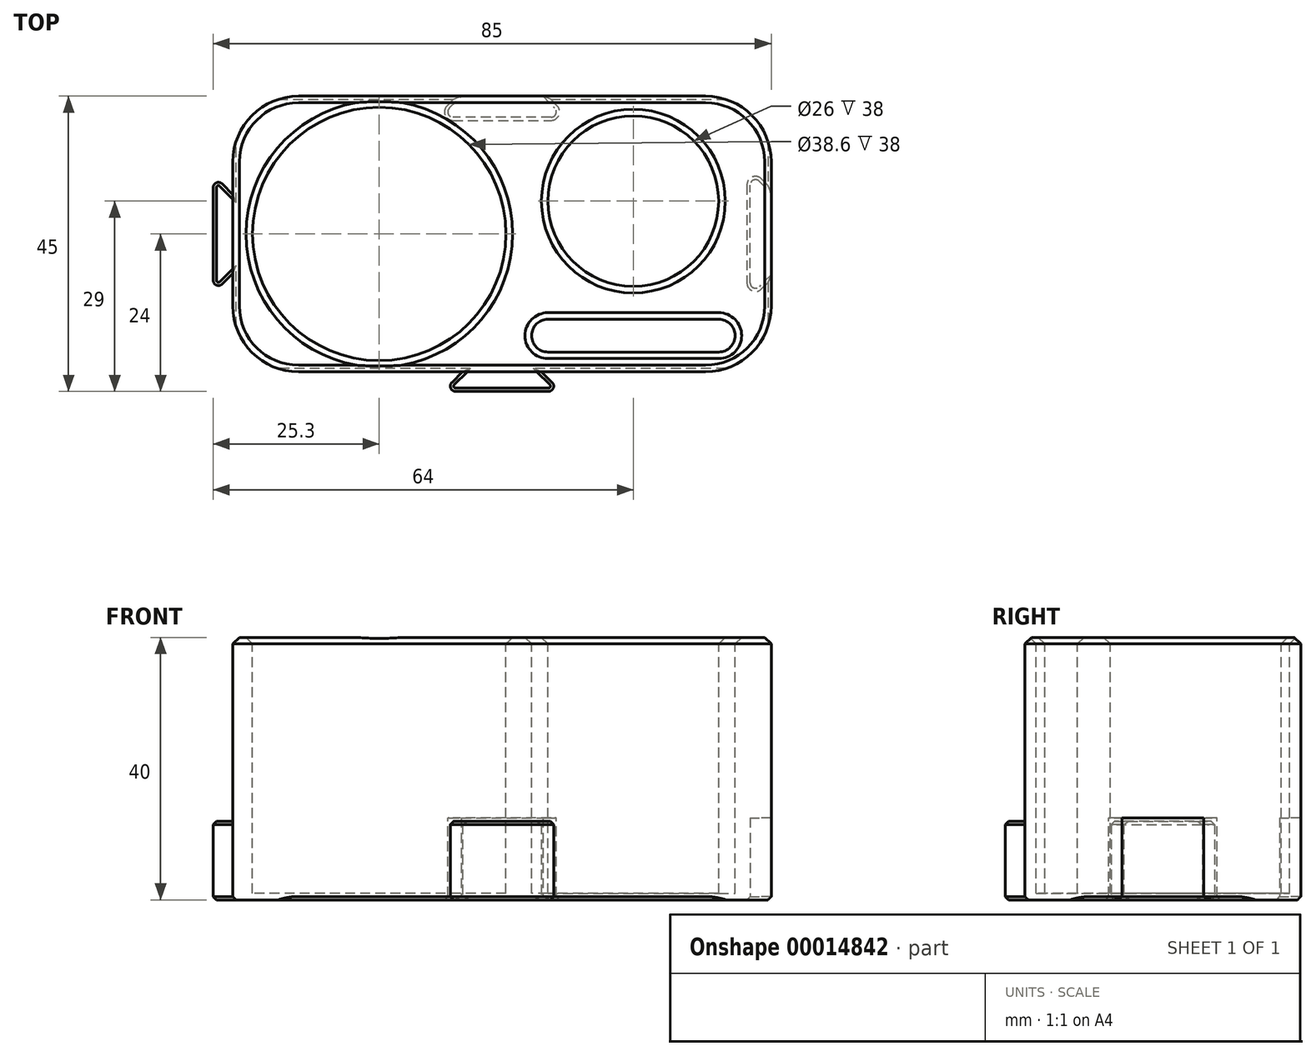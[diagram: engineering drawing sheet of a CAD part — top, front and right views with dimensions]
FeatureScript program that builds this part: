
annotation { "Feature Type Name" : "Feature", "Feature Type Description" : "" }
export const myFeature = defineFeature(function(context is Context, id is Id, definition is map)
    precondition{}
    {
        {
            var Q0;
            Q0=qCreatedBy(makeId("Top.planeOp"),FACE);
            var sketch = newSketch(context, id + "F0", { "sketchPlane" : qUnion([Q0])});
            skLineSegment(sketch, "E0.bottom", {"start": v(0, 0) * mm, "end": v(82, 0) * mm});
            skLineSegment(sketch, "E0.top", {"start": v(0, 42) * mm, "end": v(82, 42) * mm});
            skLineSegment(sketch, "E0.left", {"start": v(0, 0) * mm, "end": v(0, 42) * mm});
            skLineSegment(sketch, "E0.right", {"start": v(82, 0) * mm, "end": v(82, 42) * mm});
            skLineSegment(sketch, "E1", {"start": v(0, 21) * mm, "end": v(82, 21) * mm, "construction": true});
            skLineSegment(sketch, "E2", {"start": v(41, 42) * mm, "end": v(41, 0) * mm, "construction": true});
            skLineSegment(sketch, "E3", {"start": v(35, 0) * mm, "end": v(32, -3) * mm});
            skLineSegment(sketch, "E4", {"start": v(32, -3) * mm, "end": v(50, -3) * mm});
            skLineSegment(sketch, "E5", {"start": v(50, -3) * mm, "end": v(47, 0) * mm});
            skLineSegment(sketch, "E6", {"start": v(47.2, 42) * mm, "end": v(50.4, 38.8) * mm});
            skLineSegment(sketch, "E7", {"start": v(50.4, 38.8) * mm, "end": v(31.6, 38.8) * mm});
            skLineSegment(sketch, "E8", {"start": v(31.6, 38.8) * mm, "end": v(34.8, 42) * mm});
            skLineSegment(sketch, "E9", {"start": v(0, 15) * mm, "end": v(-3, 12) * mm});
            skLineSegment(sketch, "E10", {"start": v(-3, 12) * mm, "end": v(-3, 30) * mm});
            skLineSegment(sketch, "E11", {"start": v(-3, 30) * mm, "end": v(0, 27) * mm});
            skLineSegment(sketch, "E12", {"start": v(82, 14.8) * mm, "end": v(78.8, 11.6) * mm});
            skLineSegment(sketch, "E13", {"start": v(78.8, 11.6) * mm, "end": v(78.8, 30.4) * mm});
            skLineSegment(sketch, "E14", {"start": v(78.8, 30.4) * mm, "end": v(82, 27.2) * mm});
            skSolve(sketch);
        }
        {
            var Q0;
            {var subQ1=sQuery(id+"F0.wireOp",EDGE,"E6");Q0=makeQuery(id+"F0.imprint","IMPRINT",FACE,{"disambiguationData":[TD([[makeQuery(id+"F0.imprint","IMPRINT",EDGE,{"derivedFrom":subQ1}),-1.0]])]});}
            var Q1;
            {var subQ1=sQuery(id+"F0.wireOp",EDGE,"E12");Q1=makeQuery(id+"F0.imprint","IMPRINT",FACE,{"disambiguationData":[TD([[makeQuery(id+"F0.imprint","IMPRINT",EDGE,{"derivedFrom":subQ1}),-1.0]])]});}
            var Q2;
            {var subQ8=sQuery(id+"F0.wireOp",EDGE,"E6");Q2=makeQuery(id+"F0.imprint","IMPRINT",FACE,{"disambiguationData":[TD([[makeQuery(id+"F0.imprint","IMPRINT",EDGE,{"derivedFrom":subQ8}),1.0]])]});}
            extrude(context, id + "F1", {"entities" : qUnion([Q0, Q1, Q2]), "depth" : 40 * mm});
        }
        {
            var Q0;
            {var subQ1=sQuery(id+"F0.wireOp",EDGE,"E3");Q0=makeQuery(id+"F0.imprint","IMPRINT",FACE,{"disambiguationData":[TD([[makeQuery(id+"F0.imprint","IMPRINT",EDGE,{"derivedFrom":subQ1}),1.0]])]});}
            var Q1;
            {var subQ1=sQuery(id+"F0.wireOp",EDGE,"E9");Q1=makeQuery(id+"F0.imprint","IMPRINT",FACE,{"disambiguationData":[TD([[makeQuery(id+"F0.imprint","IMPRINT",EDGE,{"derivedFrom":subQ1}),-1.0]])]});}
            extrude(context, id + "F2", {"entities" : qUnion([Q0, Q1]), "operationType" : NewBodyOperationType.ADD, "depth" : 12 * mm});
        }
        {
            var Q0;
            {var subQ1=sQuery(id+"F0.wireOp",EDGE,"E6");Q0=makeQuery(id+"F0.imprint","IMPRINT",FACE,{"disambiguationData":[TD([[makeQuery(id+"F0.imprint","IMPRINT",EDGE,{"derivedFrom":subQ1}),-1.0]])]});}
            var Q1;
            {var subQ1=sQuery(id+"F0.wireOp",EDGE,"E12");Q1=makeQuery(id+"F0.imprint","IMPRINT",FACE,{"disambiguationData":[TD([[makeQuery(id+"F0.imprint","IMPRINT",EDGE,{"derivedFrom":subQ1}),-1.0]])]});}
            extrude(context, id + "F3", {"entities" : qUnion([Q0, Q1]), "operationType" : NewBodyOperationType.REMOVE, "depth" : 12.5 * mm});
        }
        {
            var Q0;
            Q0=makeQuery(id+"F3.boolean.opBoolean","COPY",EDGE,{"derivedFrom":makeQuery(id+"F3.opExtrude","SWEPT_EDGE",EDGE,{"disambiguationData":[OSD([sQuery(id+"F0.wireOp",EDGE,"E0.right"),sQuery(id+"F0.wireOp",EDGE,"E14")])]})});
            var Q1;
            Q1=makeQuery(id+"F3.boolean.opBoolean","COPY",EDGE,{"derivedFrom":makeQuery(id+"F3.opExtrude","SWEPT_EDGE",EDGE,{"disambiguationData":[OSD([sQuery(id+"F0.wireOp",EDGE,"E13"),sQuery(id+"F0.wireOp",EDGE,"E14")])]})});
            var Q2;
            Q2=makeQuery(id+"F3.boolean.opBoolean","COPY",EDGE,{"derivedFrom":makeQuery(id+"F3.opExtrude","SWEPT_EDGE",EDGE,{"disambiguationData":[OSD([sQuery(id+"F0.wireOp",EDGE,"E0.right"),sQuery(id+"F0.wireOp",EDGE,"E12")])]})});
            var Q3;
            Q3=makeQuery(id+"F2.opExtrude","SWEPT_EDGE",EDGE,{"disambiguationData":[OSD([sQuery(id+"F0.wireOp",EDGE,"E4"),sQuery(id+"F0.wireOp",EDGE,"E5")])]});
            var Q4;
            Q4=makeQuery(id+"F3.boolean.opBoolean","COPY",EDGE,{"derivedFrom":makeQuery(id+"F3.opExtrude","SWEPT_EDGE",EDGE,{"disambiguationData":[OSD([sQuery(id+"F0.wireOp",EDGE,"E12"),sQuery(id+"F0.wireOp",EDGE,"E13")])]})});
            var Q5;
            Q5=makeQuery(id+"F3.boolean.opBoolean","COPY",EDGE,{"derivedFrom":makeQuery(id+"F3.opExtrude","SWEPT_EDGE",EDGE,{"disambiguationData":[OSD([sQuery(id+"F0.wireOp",EDGE,"E0.top"),sQuery(id+"F0.wireOp",EDGE,"E8")])]})});
            var Q6;
            Q6=makeQuery(id+"F3.boolean.opBoolean","COPY",EDGE,{"derivedFrom":makeQuery(id+"F3.opExtrude","SWEPT_EDGE",EDGE,{"disambiguationData":[OSD([sQuery(id+"F0.wireOp",EDGE,"E0.top"),sQuery(id+"F0.wireOp",EDGE,"E6")])]})});
            var Q7;
            Q7=makeQuery(id+"F3.boolean.opBoolean","COPY",EDGE,{"derivedFrom":makeQuery(id+"F3.opExtrude","SWEPT_EDGE",EDGE,{"disambiguationData":[OSD([sQuery(id+"F0.wireOp",EDGE,"E7"),sQuery(id+"F0.wireOp",EDGE,"E8")])]})});
            var Q8;
            Q8=makeQuery(id+"F3.boolean.opBoolean","COPY",EDGE,{"derivedFrom":makeQuery(id+"F3.opExtrude","SWEPT_EDGE",EDGE,{"disambiguationData":[OSD([sQuery(id+"F0.wireOp",EDGE,"E6"),sQuery(id+"F0.wireOp",EDGE,"E7")])]})});
            var Q9;
            Q9=makeQuery(id+"F2.opExtrude","SWEPT_EDGE",EDGE,{"disambiguationData":[OSD([sQuery(id+"F0.wireOp",EDGE,"E10"),sQuery(id+"F0.wireOp",EDGE,"E11")])]});
            var Q10;
            Q10=makeQuery(id+"F2.opExtrude","SWEPT_EDGE",EDGE,{"disambiguationData":[OSD([sQuery(id+"F0.wireOp",EDGE,"E0.left"),sQuery(id+"F0.wireOp",EDGE,"E11")])]});
            var Q11;
            Q11=makeQuery(id+"F2.opExtrude","SWEPT_EDGE",EDGE,{"disambiguationData":[OSD([sQuery(id+"F0.wireOp",EDGE,"E0.left"),sQuery(id+"F0.wireOp",EDGE,"E9")])]});
            var Q12;
            Q12=makeQuery(id+"F2.opExtrude","SWEPT_EDGE",EDGE,{"disambiguationData":[OSD([sQuery(id+"F0.wireOp",EDGE,"E9"),sQuery(id+"F0.wireOp",EDGE,"E10")])]});
            var Q13;
            Q13=makeQuery(id+"F2.opExtrude","SWEPT_EDGE",EDGE,{"disambiguationData":[OSD([sQuery(id+"F0.wireOp",EDGE,"E3"),sQuery(id+"F0.wireOp",EDGE,"E4")])]});
            var Q14;
            Q14=makeQuery(id+"F2.opExtrude","SWEPT_EDGE",EDGE,{"disambiguationData":[OSD([sQuery(id+"F0.wireOp",EDGE,"E0.bottom"),sQuery(id+"F0.wireOp",EDGE,"E3")])]});
            var Q15;
            Q15=makeQuery(id+"F2.opExtrude","SWEPT_EDGE",EDGE,{"disambiguationData":[OSD([sQuery(id+"F0.wireOp",EDGE,"E0.bottom"),sQuery(id+"F0.wireOp",EDGE,"E5")])]});
            fillet(context, id + "F4", {"entities" : qUnion([Q0, Q1, Q2, Q3, Q4, Q5, Q6, Q7, Q8, Q9, Q10, Q11, Q12, Q13, Q14, Q15]), "radius" : .8 * mm, "tangentPropagation" : true, "allowEdgeOverflow" : false});
        }
        {
            var Q0;
            Q0=makeQuery(id+"F2.opExtrude","CAP_EDGE",EDGE,{"disambiguationData":[OSD([sQuery(id+"F0.wireOp",EDGE,"E4")])],"isStart":false});
            var Q1;
            Q1=makeQuery(id+"F2.opExtrude","CAP_EDGE",EDGE,{"disambiguationData":[OSD([sQuery(id+"F0.wireOp",EDGE,"E10")])],"isStart":false});
            chamfer(context, id + "F5", {"entities" : qUnion([Q0, Q1]), "width" : .5 * mm, "tangentPropagation" : true});
        }
        {
            var Q0;
            {var subQ0=sQuery(id+"F0.wireOp",EDGE,"E0.bottom");var subQ1=sQuery(id+"F0.wireOp",EDGE,"E0.left");Q0=makeQuery(id+"F2.boolean.opBoolean","MERGE",FACE,{"derivedFrom":[makeQuery(id+"F1.opExtrude","CAP_FACE",FACE,{"disambiguationData":[OSD([subQ0,sQuery(id+"F0.wireOp",EDGE,"E0.top"),subQ1,sQuery(id+"F0.wireOp",EDGE,"E0.right")])],"isStart":true}),makeQuery(id+"F2.opExtrude","CAP_FACE",FACE,{"disambiguationData":[OSD([subQ0,sQuery(id+"F0.wireOp",EDGE,"E3"),sQuery(id+"F0.wireOp",EDGE,"E4"),sQuery(id+"F0.wireOp",EDGE,"E5")])],"isStart":true}),makeQuery(id+"F2.opExtrude","CAP_FACE",FACE,{"disambiguationData":[OSD([subQ1,sQuery(id+"F0.wireOp",EDGE,"E9"),sQuery(id+"F0.wireOp",EDGE,"E10"),sQuery(id+"F0.wireOp",EDGE,"E11")])],"isStart":true})]});}
            chamfer(context, id + "F6", {"entities" : qUnion([Q0]), "width" : .5 * mm, "tangentPropagation" : true});
        }
        {
            var Q0;
            Q0=makeQuery(id+"F1.opExtrude","CAP_FACE",FACE,{"disambiguationData":[OSD([sQuery(id+"F0.wireOp",EDGE,"E0.bottom"),sQuery(id+"F0.wireOp",EDGE,"E0.top"),sQuery(id+"F0.wireOp",EDGE,"E0.left"),sQuery(id+"F0.wireOp",EDGE,"E0.right")])],"isStart":false});
            var sketch = newSketch(context, id + "F7", { "sketchPlane" : qUnion([Q0])});
            skLineSegment(sketch, "E15", {"start": v(0, 21) * mm, "end": v(82, 21) * mm, "construction": true});
            skCircle(sketch, "E16", {"center": v(22.3, 21) * mm, "radius": 19.3 * mm});
            skLineSegment(sketch, "E17", {"start": v(48, 8) * mm, "end": v(74, 8) * mm});
            skLineSegment(sketch, "E18", {"start": v(74, 3) * mm, "end": v(48, 3) * mm});
            skArc(sketch, "E19", {"start": v(48, 8) * mm, "mid": v(45.5, 5.5) * mm, "end": v(48, 3) * mm});
            skArc(sketch, "E20", {"start": v(74, 3) * mm, "mid": v(76.5, 5.5) * mm, "end": v(74, 8) * mm});
            skCircle(sketch, "E21", {"center": v(61, 26) * mm, "radius": 13 * mm});
            skSolve(sketch);
        }
        {
            var Q0;
            Q0=makeQuery(id+"F7.imprint","IMPRINT",FACE,{"disambiguationData":[TD([[makeQuery(id+"F7.imprint","IMPRINT",EDGE,{"derivedFrom":sQuery(id+"F7.wireOp",EDGE,"E16")}),1.0]])]});
            var Q1;
            Q1=makeQuery(id+"F7.imprint","IMPRINT",FACE,{"disambiguationData":[TD([[makeQuery(id+"F7.imprint","IMPRINT",EDGE,{"derivedFrom":sQuery(id+"F7.wireOp",EDGE,"E21")}),1.0]])]});
            var Q2;
            Q2=makeQuery(id+"F7.imprint","IMPRINT",FACE,{"disambiguationData":[TD([[makeQuery(id+"F7.imprint","IMPRINT",EDGE,{"derivedFrom":sQuery(id+"F7.wireOp",EDGE,"E17")}),-1.0]])]});
            extrude(context, id + "F8", {"entities" : qUnion([Q0, Q1, Q2]), "operationType" : NewBodyOperationType.REMOVE, "oppositeDirection" : true, "depth" : 39 * mm});
        }
        {
            var Q0;
            Q0=makeQuery(id+"F1.opExtrude","SWEPT_EDGE",EDGE,{"disambiguationData":[OSD([sQuery(id+"F0.wireOp",EDGE,"E0.bottom"),sQuery(id+"F0.wireOp",EDGE,"E0.left")])]});
            var Q1;
            Q1=makeQuery(id+"F1.opExtrude","SWEPT_EDGE",EDGE,{"disambiguationData":[OSD([sQuery(id+"F0.wireOp",EDGE,"E0.bottom"),sQuery(id+"F0.wireOp",EDGE,"E0.right")])]});
            var Q2;
            Q2=makeQuery(id+"F1.opExtrude","SWEPT_EDGE",EDGE,{"disambiguationData":[OSD([sQuery(id+"F0.wireOp",EDGE,"E0.top"),sQuery(id+"F0.wireOp",EDGE,"E0.right")])]});
            var Q3;
            Q3=makeQuery(id+"F1.opExtrude","SWEPT_EDGE",EDGE,{"disambiguationData":[OSD([sQuery(id+"F0.wireOp",EDGE,"E0.top"),sQuery(id+"F0.wireOp",EDGE,"E0.left")])]});
            fillet(context, id + "F9", {"entities" : qUnion([Q0, Q1, Q2, Q3]), "radius" : 10 * mm, "tangentPropagation" : true, "allowEdgeOverflow" : false});
        }
        {
            var Q0;
            Q0=makeQuery(id+"F1.opExtrude","CAP_FACE",FACE,{"disambiguationData":[OSD([sQuery(id+"F0.wireOp",EDGE,"E0.bottom"),sQuery(id+"F0.wireOp",EDGE,"E0.top"),sQuery(id+"F0.wireOp",EDGE,"E0.left"),sQuery(id+"F0.wireOp",EDGE,"E0.right")])],"isStart":false});
            chamfer(context, id + "F10", {"entities" : qUnion([Q0]), "width" : 1 * mm, "tangentPropagation" : true});
        }
    });
